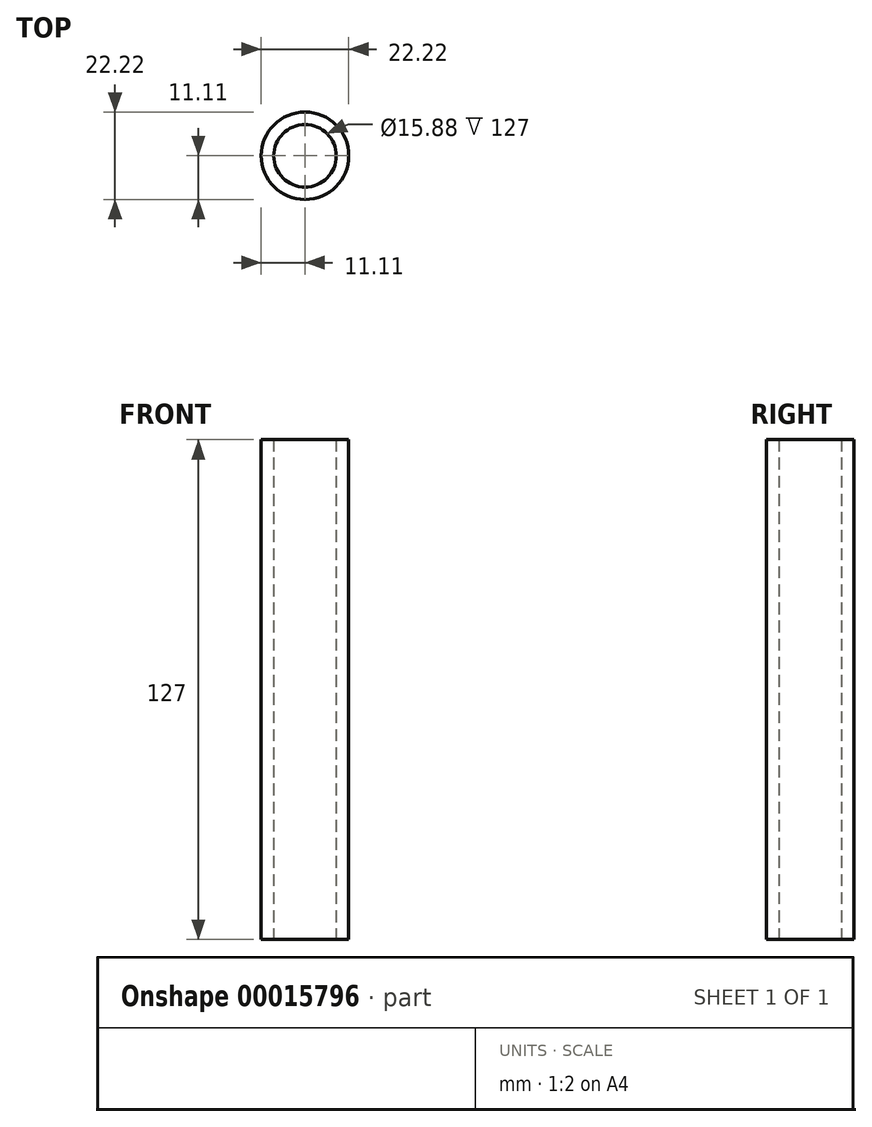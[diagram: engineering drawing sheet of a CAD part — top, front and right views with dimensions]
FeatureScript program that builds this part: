
annotation { "Feature Type Name" : "Feature", "Feature Type Description" : "" }
export const myFeature = defineFeature(function(context is Context, id is Id, definition is map)
    precondition{}
    {
        {
            var Q0;
            Q0=qCreatedBy(makeId("Top.planeOp"),FACE);
            var sketch = newSketch(context, id + "F0", { "sketchPlane" : qUnion([Q0])});
            skCircle(sketch, "E0", {"center": v(0, 0) * mm, "radius": 11.11 * mm});
            skCircle(sketch, "E1", {"center": v(0, 0) * mm, "radius": 7.94 * mm});
            skSolve(sketch);
        }
        {
            var Q0;
            Q0=qSketchRegion(id+"F0",true);
            extrude(context, id + "F1", {"entities" : qUnion([Q0]), "depth" : 127 * mm});
        }
    });
